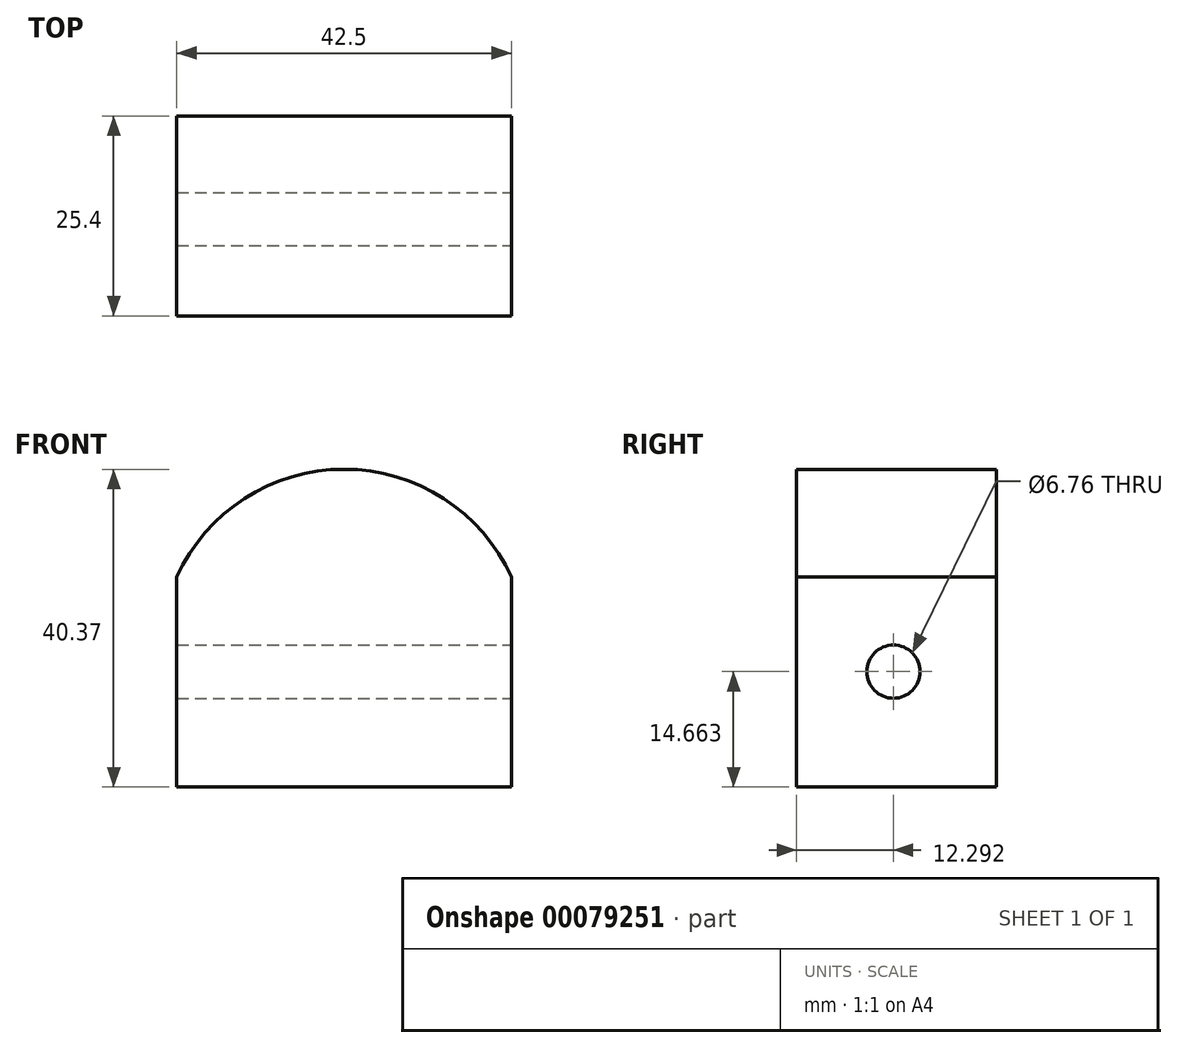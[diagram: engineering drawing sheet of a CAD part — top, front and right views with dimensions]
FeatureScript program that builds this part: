
annotation { "Feature Type Name" : "Feature", "Feature Type Description" : "" }
export const myFeature = defineFeature(function(context is Context, id is Id, definition is map)
    precondition{}
    {
        {
            var Q0;
            Q0=qCreatedBy(makeId("Front.planeOp"),FACE);
            var sketch = newSketch(context, id + "F0", { "sketchPlane" : qUnion([Q0])});
            skLineSegment(sketch, "E0", {"start": v(0, 0) * mm, "end": v(-42.5, 0) * mm});
            skLineSegment(sketch, "E1", {"start": v(-42.5, 0) * mm, "end": v(-42.5, 26.67) * mm});
            skLineSegment(sketch, "E2", {"start": v(0, 26.67) * mm, "end": v(0, 0) * mm});
            skArc(sketch, "E3", {"start": v(0, 26.67) * mm, "mid": v(-21.25, 40.37) * mm, "end": v(-42.5, 26.67) * mm});
            skSolve(sketch);
        }
        {
            var Q0;
            Q0=makeQuery(id+"F0.imprint","IMPRINT",FACE,{"disambiguationData":[TD([[makeQuery(id+"F0.imprint","IMPRINT",EDGE,{"derivedFrom":sQuery(id+"F0.wireOp",EDGE,"E0")}),-1.0]])]});
            extrude(context, id + "F1", {"entities" : qUnion([Q0]), "oppositeDirection" : true, "depth" : 25.4 * mm});
        }
        {
            var Q0;
            Q0=makeQuery(id+"F1.opExtrude","SWEPT_FACE",FACE,{"disambiguationData":[OSD([sQuery(id+"F0.wireOp",EDGE,"E2")])]});
            var sketch = newSketch(context, id + "F2", { "sketchPlane" : qUnion([Q0])});
            skCircle(sketch, "E4", {"center": v(12.3, 14.66) * mm, "radius": 6.35 * mm});
            skSolve(sketch);
        }
        {
            var Q0;
            Q0=sQuery(id+"F2.wireOp",VERTEX,"E4.center");
            var Q1;
            Q1=makeQuery(id+"F1.opExtrude","SWEPT_BODY",BODY,{"disambiguationData":[OSD([sQuery(id+"F0.wireOp",EDGE,"E0"),sQuery(id+"F0.wireOp",EDGE,"E1"),sQuery(id+"F0.wireOp",EDGE,"E2"),sQuery(id+"F0.wireOp",EDGE,"E3")])]});
            hole(context, id + "F3", {"style" : HoleStyle.SIMPLE, "endStyle" : HoleEndStyle.THROUGH, "standardTappedOrClearance" : lookupTablePath({ "standard" : "ANSI", "fit" : "Normal (ASME)", "size" : "1/4", "type" : "Clearance" }), "standardBlindInLast" : lookupTablePath({ "fit" : "Free", "standard" : "ANSI", "size" : "1/4", "type" : "Clearance" }), "holeDiameter" : 6.76 * mm, "locations" : qUnion([Q0]), "scope" : qUnion([Q1]), "isTappedThrough" : true});
        }
    });
